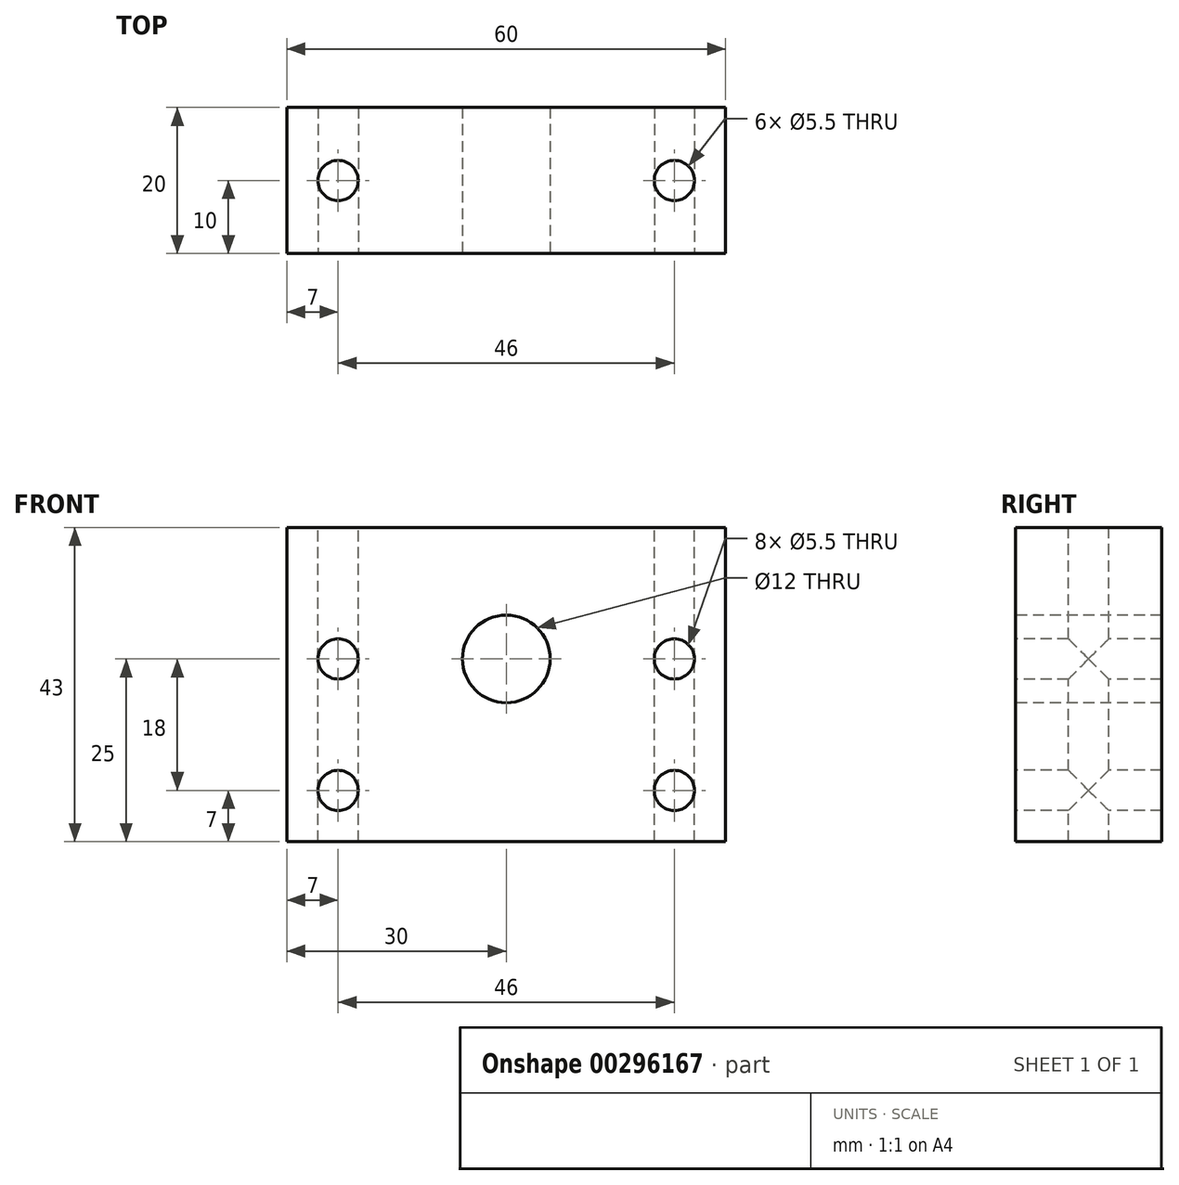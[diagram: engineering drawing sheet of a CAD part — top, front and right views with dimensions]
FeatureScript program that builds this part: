
annotation { "Feature Type Name" : "Feature", "Feature Type Description" : "" }
export const myFeature = defineFeature(function(context is Context, id is Id, definition is map)
    precondition{}
    {
        {
            var Q0;
            Q0=qCreatedBy(makeId("Front.planeOp"),FACE);
            var sketch = newSketch(context, id + "F0", { "sketchPlane" : qUnion([Q0])});
            skLineSegment(sketch, "E0.bottom", {"start": v(30, 21.5) * mm, "end": v(-30, 21.5) * mm});
            skLineSegment(sketch, "E0.top", {"start": v(30, -21.5) * mm, "end": v(-30, -21.5) * mm});
            skLineSegment(sketch, "E0.left", {"start": v(30, 21.5) * mm, "end": v(30, -21.5) * mm});
            skLineSegment(sketch, "E0.right", {"start": v(-30, 21.5) * mm, "end": v(-30, -21.5) * mm});
            skPoint(sketch, "E0.middle", {"position": v(0, 0) * mm});
            skLineSegment(sketch, "E1", {"start": v(0, -21.5) * mm, "end": v(0, 3.5) * mm, "construction": true});
            skPoint(sketch, "E1.endSnap0", {"position": v(0, -21.5) * mm});
            skCircle(sketch, "E2", {"center": v(0, 3.5) * mm, "radius": 6 * mm});
            skSolve(sketch);
        }
        {
            var Q0;
            Q0=qSketchRegion(id+"F0",true);
            extrude(context, id + "F1", {"entities" : qUnion([Q0]), "oppositeDirection" : true, "depth" : 20 * mm});
        }
        {
            var Q0;
            Q0=makeQuery(id+"F1.opExtrude","SWEPT_FACE",FACE,{"disambiguationData":[OSD([sQuery(id+"F0.wireOp",EDGE,"E0.bottom")])]});
            var sketch = newSketch(context, id + "F2", { "sketchPlane" : qUnion([Q0])});
            skLineSegment(sketch, "E3.bottom", {"start": v(23, 25) * mm, "end": v(-23, 25) * mm, "construction": true});
            skLineSegment(sketch, "E3.top", {"start": v(23, -25) * mm, "end": v(-23, -25) * mm, "construction": true});
            skLineSegment(sketch, "E3.left", {"start": v(23, 25) * mm, "end": v(23, -25) * mm, "construction": true});
            skLineSegment(sketch, "E3.right", {"start": v(-23, 25) * mm, "end": v(-23, -25) * mm, "construction": true});
            skPoint(sketch, "E3.middle", {"position": v(0, 0) * mm});
            skLineSegment(sketch, "E4", {"start": v(-30, 10) * mm, "end": v(30, 10) * mm, "construction": true});
            skCircle(sketch, "E5", {"center": v(-23, 10) * mm, "radius": 2.75 * mm});
            skCircle(sketch, "E6", {"center": v(23, 10) * mm, "radius": 2.75 * mm});
            skSolve(sketch);
        }
        {
            var Q0;
            Q0=qSketchRegion(id+"F2",true);
            extrude(context, id + "F3", {"entities" : qUnion([Q0]), "operationType" : NewBodyOperationType.REMOVE, "endBound" : BoundingType.THROUGH_ALL, "oppositeDirection" : true, "depth" : 25 * mm});
        }
        {
            var Q0;
            Q0=makeQuery(id+"F1.opExtrude","CAP_FACE",FACE,{"disambiguationData":[OSD([sQuery(id+"F0.wireOp",EDGE,"E0.bottom"),sQuery(id+"F0.wireOp",EDGE,"E0.top"),sQuery(id+"F0.wireOp",EDGE,"E0.left"),sQuery(id+"F0.wireOp",EDGE,"E0.right"),sQuery(id+"F0.wireOp",EDGE,"E2")])],"isStart":true});
            var sketch = newSketch(context, id + "F4", { "sketchPlane" : qUnion([Q0])});
            skLineSegment(sketch, "E7", {"start": v(-30, -21.5) * mm, "end": v(-30, 3.5) * mm, "construction": true});
            skLineSegment(sketch, "E8", {"start": v(-30, 3.5) * mm, "end": v(30, 3.5) * mm, "construction": true});
            skCircle(sketch, "E9", {"center": v(-23, 3.5) * mm, "radius": 2.75 * mm});
            skCircle(sketch, "E10", {"center": v(23, 3.5) * mm, "radius": 2.75 * mm});
            skLineSegment(sketch, "E11", {"start": v(0, -21.5) * mm, "end": v(0, 21.5) * mm, "construction": true});
            skLineSegment(sketch, "E12", {"start": v(-30, 3.5) * mm, "end": v(-30, -14.5) * mm, "construction": true});
            skLineSegment(sketch, "E13", {"start": v(-30, -14.5) * mm, "end": v(30, -14.5) * mm, "construction": true});
            skCircle(sketch, "E14", {"center": v(-23, -14.5) * mm, "radius": 2.75 * mm});
            skCircle(sketch, "E15", {"center": v(23, -14.5) * mm, "radius": 2.75 * mm});
            skSolve(sketch);
        }
        {
            var Q0;
            Q0=makeQuery(id+"F4.imprint","IMPRINT",FACE,{"disambiguationData":[TD([[makeQuery(id+"F4.imprint","IMPRINT",EDGE,{"derivedFrom":sQuery(id+"F4.wireOp",EDGE,"E10")}),1.0]])]});
            var Q1;
            Q1=makeQuery(id+"F4.imprint","IMPRINT",FACE,{"disambiguationData":[TD([[makeQuery(id+"F4.imprint","IMPRINT",EDGE,{"derivedFrom":sQuery(id+"F4.wireOp",EDGE,"E14")}),1.0]])]});
            var Q2;
            Q2=makeQuery(id+"F4.imprint","IMPRINT",FACE,{"disambiguationData":[TD([[makeQuery(id+"F4.imprint","IMPRINT",EDGE,{"derivedFrom":sQuery(id+"F4.wireOp",EDGE,"E15")}),1.0]])]});
            var Q3;
            Q3=makeQuery(id+"F4.imprint","IMPRINT",FACE,{"disambiguationData":[TD([[makeQuery(id+"F4.imprint","IMPRINT",EDGE,{"derivedFrom":sQuery(id+"F4.wireOp",EDGE,"E9")}),1.0]])]});
            extrude(context, id + "F5", {"entities" : qUnion([Q0, Q1, Q2, Q3]), "operationType" : NewBodyOperationType.REMOVE, "endBound" : BoundingType.THROUGH_ALL, "oppositeDirection" : true, "depth" : 25 * mm});
        }
    });
